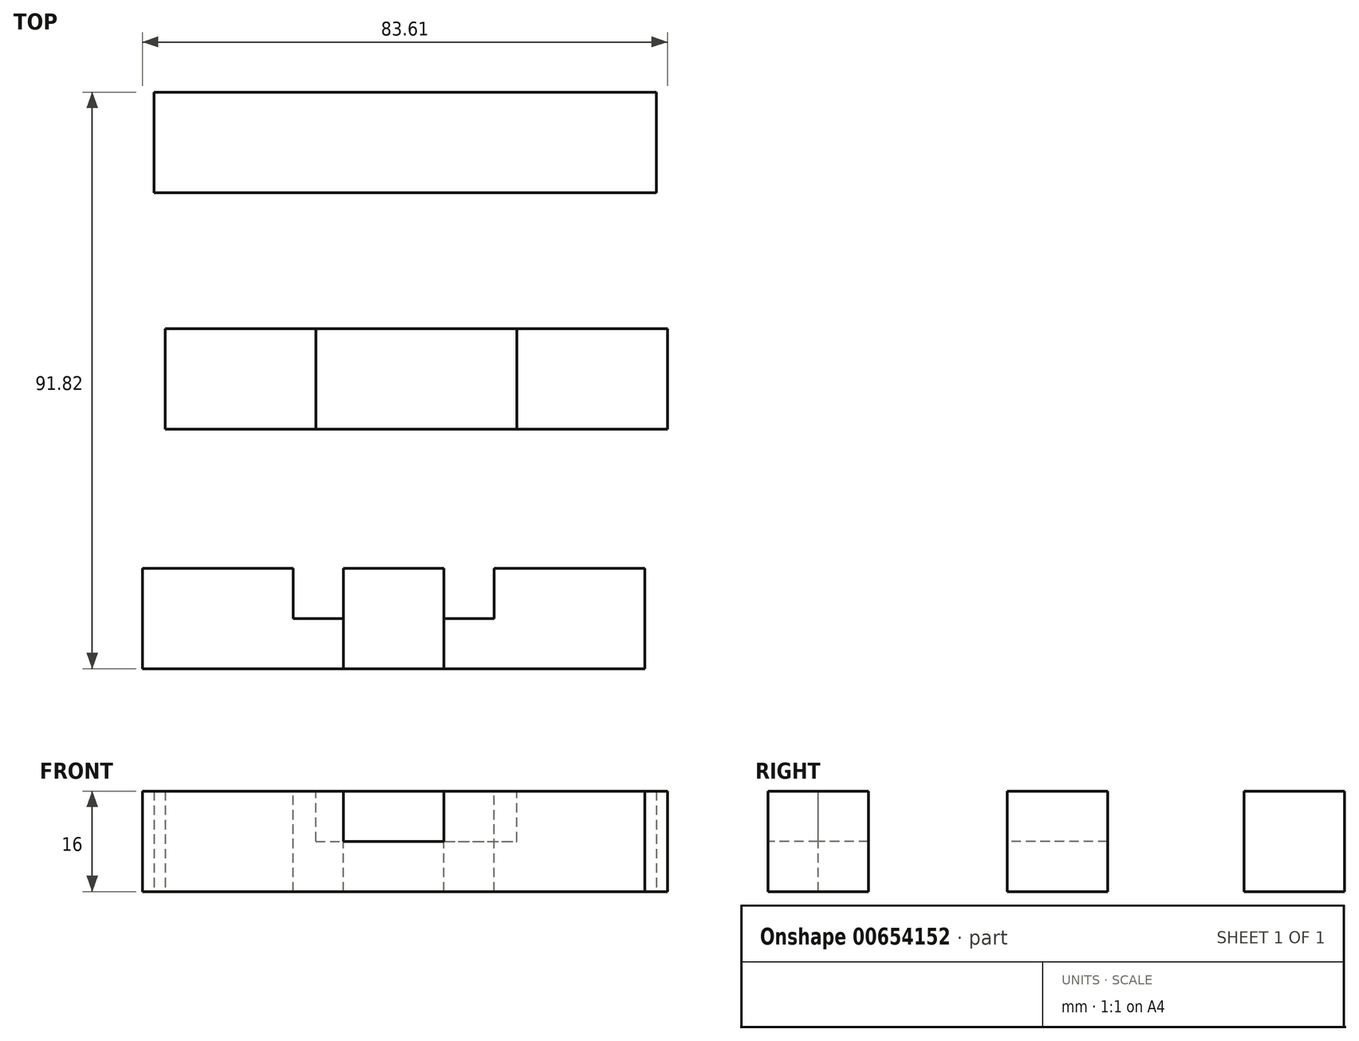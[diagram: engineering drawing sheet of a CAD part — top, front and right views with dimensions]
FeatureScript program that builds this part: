
annotation { "Feature Type Name" : "Feature", "Feature Type Description" : "" }
export const myFeature = defineFeature(function(context is Context, id is Id, definition is map)
    precondition{}
    {
        {
            var Q0;
            Q0=qCreatedBy(makeId("Top.planeOp"),FACE);
            var sketch = newSketch(context, id + "F0", { "sketchPlane" : qUnion([Q0])});
            skLineSegment(sketch, "E0.bottom", {"start": v(-37.25, 40.55) * mm, "end": v(42.75, 40.55) * mm});
            skLineSegment(sketch, "E0.top", {"start": v(-37.25, 24.55) * mm, "end": v(42.75, 24.55) * mm});
            skLineSegment(sketch, "E0.left", {"start": v(-37.25, 40.55) * mm, "end": v(-37.25, 24.55) * mm});
            skLineSegment(sketch, "E0.right", {"start": v(42.75, 40.55) * mm, "end": v(42.75, 24.55) * mm});
            skLineSegment(sketch, "E1.bottom", {"start": v(-35.5, 2.84) * mm, "end": v(44.5, 2.84) * mm});
            skLineSegment(sketch, "E1.top", {"start": v(-35.5, -13.16) * mm, "end": v(44.5, -13.16) * mm});
            skLineSegment(sketch, "E1.left", {"start": v(-35.5, 2.84) * mm, "end": v(-35.5, -13.16) * mm});
            skLineSegment(sketch, "E1.right", {"start": v(44.5, 2.84) * mm, "end": v(44.5, -13.16) * mm});
            skLineSegment(sketch, "E2.bottom", {"start": v(-39.1, -35.27) * mm, "end": v(40.9, -35.27) * mm});
            skLineSegment(sketch, "E2.top", {"start": v(-39.1, -51.27) * mm, "end": v(40.9, -51.27) * mm});
            skLineSegment(sketch, "E2.left", {"start": v(-39.1, -35.27) * mm, "end": v(-39.1, -51.27) * mm});
            skLineSegment(sketch, "E2.right", {"start": v(40.9, -35.27) * mm, "end": v(40.9, -51.27) * mm});
            skSolve(sketch);
        }
        {
            var Q0;
            Q0=makeQuery(id+"F0.imprint","IMPRINT",FACE,{"disambiguationData":[TD([[makeQuery(id+"F0.imprint","IMPRINT",EDGE,{"derivedFrom":sQuery(id+"F0.wireOp",EDGE,"E0.bottom")}),-1.0]])]});
            var Q1;
            Q1=makeQuery(id+"F0.imprint","IMPRINT",FACE,{"disambiguationData":[TD([[makeQuery(id+"F0.imprint","IMPRINT",EDGE,{"derivedFrom":sQuery(id+"F0.wireOp",EDGE,"E1.bottom")}),-1.0]])]});
            var Q2;
            Q2=makeQuery(id+"F0.imprint","IMPRINT",FACE,{"disambiguationData":[TD([[makeQuery(id+"F0.imprint","IMPRINT",EDGE,{"derivedFrom":sQuery(id+"F0.wireOp",EDGE,"E2.bottom")}),-1.0]])]});
            extrude(context, id + "F1", {"entities" : qUnion([Q0, Q1, Q2]), "depth" : 16 * mm, "offsetDistance" : 25 * mm});
        }
        {
            var Q0;
            Q0=makeQuery(id+"F1.opExtrude","CAP_FACE",FACE,{"disambiguationData":[OSD([sQuery(id+"F0.wireOp",EDGE,"E1.bottom"),sQuery(id+"F0.wireOp",EDGE,"E1.top"),sQuery(id+"F0.wireOp",EDGE,"E1.left"),sQuery(id+"F0.wireOp",EDGE,"E1.right")])],"isStart":false});
            var sketch = newSketch(context, id + "F2", { "sketchPlane" : qUnion([Q0])});
            skLineSegment(sketch, "E3.bottom", {"start": v(-11.5, 2.84) * mm, "end": v(20.5, 2.84) * mm});
            skLineSegment(sketch, "E3.top", {"start": v(-11.5, -13.16) * mm, "end": v(20.5, -13.16) * mm});
            skLineSegment(sketch, "E3.left", {"start": v(-11.5, 2.84) * mm, "end": v(-11.5, -13.16) * mm});
            skLineSegment(sketch, "E3.right", {"start": v(20.5, 2.84) * mm, "end": v(20.5, -13.16) * mm});
            skSolve(sketch);
        }
        {
            var Q0;
            Q0=makeQuery(id+"F2.imprint","IMPRINT",FACE,{"disambiguationData":[TD([[makeQuery(id+"F2.imprint","IMPRINT",EDGE,{"derivedFrom":sQuery(id+"F2.wireOp",EDGE,"E3.bottom")}),-1.0]])]});
            extrude(context, id + "F3", {"entities" : qUnion([Q0]), "operationType" : NewBodyOperationType.REMOVE, "oppositeDirection" : true, "depth" : 8 * mm, "offsetDistance" : 25 * mm});
        }
        {
            var Q0;
            Q0=makeQuery(id+"F1.opExtrude","CAP_FACE",FACE,{"disambiguationData":[OSD([sQuery(id+"F0.wireOp",EDGE,"E2.bottom"),sQuery(id+"F0.wireOp",EDGE,"E2.top"),sQuery(id+"F0.wireOp",EDGE,"E2.left"),sQuery(id+"F0.wireOp",EDGE,"E2.right")])],"isStart":false});
            var sketch = newSketch(context, id + "F4", { "sketchPlane" : qUnion([Q0])});
            skLineSegment(sketch, "E4.bottom", {"start": v(-7.1, -35.27) * mm, "end": v(8.9, -35.27) * mm});
            skLineSegment(sketch, "E4.top", {"start": v(-7.1, -51.27) * mm, "end": v(8.9, -51.27) * mm});
            skLineSegment(sketch, "E4.left", {"start": v(-7.1, -35.27) * mm, "end": v(-7.1, -51.27) * mm});
            skLineSegment(sketch, "E4.right", {"start": v(8.9, -35.27) * mm, "end": v(8.9, -51.27) * mm});
            skSolve(sketch);
        }
        {
            var Q0;
            Q0=makeQuery(id+"F4.imprint","IMPRINT",FACE,{"disambiguationData":[TD([[makeQuery(id+"F4.imprint","IMPRINT",EDGE,{"derivedFrom":sQuery(id+"F4.wireOp",EDGE,"E4.bottom")}),-1.0]])]});
            extrude(context, id + "F5", {"entities" : qUnion([Q0]), "operationType" : NewBodyOperationType.REMOVE, "oppositeDirection" : true, "depth" : 8 * mm, "offsetDistance" : 25 * mm});
        }
        {
            var Q0;
            {var subQ0=sQuery(id+"F0.wireOp",EDGE,"E2.bottom");var subQ1=sQuery(id+"F0.wireOp",EDGE,"E2.right");var subQ2=sQuery(id+"F0.wireOp",EDGE,"E2.top");Q0=makeQuery(id+"F5.boolean.opBoolean","SPLIT",FACE,{"disambiguationData":[TD([makeQuery(id+"F1.opExtrude","SWEPT_FACE",FACE,{"disambiguationData":[OSD([subQ1])]})])],"derivedFrom":makeQuery(id+"F1.opExtrude","CAP_FACE",FACE,{"disambiguationData":[OSD([subQ0,subQ2,sQuery(id+"F0.wireOp",EDGE,"E2.left"),subQ1])],"isStart":false})});}
            var sketch = newSketch(context, id + "F6", { "sketchPlane" : qUnion([Q0])});
            skLineSegment(sketch, "E5.bottom", {"start": v(8.9, -35.27) * mm, "end": v(16.9, -35.27) * mm});
            skLineSegment(sketch, "E5.top", {"start": v(8.9, -43.27) * mm, "end": v(16.9, -43.27) * mm});
            skLineSegment(sketch, "E5.left", {"start": v(8.9, -35.27) * mm, "end": v(8.9, -43.27) * mm});
            skLineSegment(sketch, "E5.right", {"start": v(16.9, -35.27) * mm, "end": v(16.9, -43.27) * mm});
            skSolve(sketch);
        }
        {
            var Q0;
            Q0=makeQuery(id+"F6.imprint","IMPRINT",FACE,{"disambiguationData":[TD([[makeQuery(id+"F6.imprint","IMPRINT",EDGE,{"derivedFrom":sQuery(id+"F6.wireOp",EDGE,"E5.bottom")}),-1.0]])]});
            extrude(context, id + "F7", {"entities" : qUnion([Q0]), "operationType" : NewBodyOperationType.REMOVE, "oppositeDirection" : true, "depth" : 16 * mm, "offsetDistance" : 25 * mm});
        }
        {
            var Q0;
            {var subQ0=sQuery(id+"F0.wireOp",EDGE,"E2.bottom");var subQ1=sQuery(id+"F0.wireOp",EDGE,"E2.top");var subQ2=sQuery(id+"F0.wireOp",EDGE,"E2.left");Q0=makeQuery(id+"F5.boolean.opBoolean","SPLIT",FACE,{"disambiguationData":[TD([makeQuery(id+"F1.opExtrude","SWEPT_FACE",FACE,{"disambiguationData":[OSD([subQ2])]})])],"derivedFrom":makeQuery(id+"F1.opExtrude","CAP_FACE",FACE,{"disambiguationData":[OSD([subQ0,subQ1,subQ2,sQuery(id+"F0.wireOp",EDGE,"E2.right")])],"isStart":false})});}
            var sketch = newSketch(context, id + "F8", { "sketchPlane" : qUnion([Q0])});
            skLineSegment(sketch, "E6.bottom", {"start": v(-7.1, -35.27) * mm, "end": v(-15.1, -35.27) * mm});
            skLineSegment(sketch, "E6.top", {"start": v(-7.1, -43.27) * mm, "end": v(-15.1, -43.27) * mm});
            skLineSegment(sketch, "E6.left", {"start": v(-7.1, -35.27) * mm, "end": v(-7.1, -43.27) * mm});
            skLineSegment(sketch, "E6.right", {"start": v(-15.1, -35.27) * mm, "end": v(-15.1, -43.27) * mm});
            skSolve(sketch);
        }
        {
            var Q0;
            Q0=makeQuery(id+"F8.imprint","IMPRINT",FACE,{"disambiguationData":[TD([[makeQuery(id+"F8.imprint","IMPRINT",EDGE,{"derivedFrom":sQuery(id+"F8.wireOp",EDGE,"E6.bottom")}),-1.0]])]});
            extrude(context, id + "F9", {"entities" : qUnion([Q0]), "operationType" : NewBodyOperationType.REMOVE, "oppositeDirection" : true, "depth" : 25 * mm, "offsetDistance" : 25 * mm});
        }
    });
